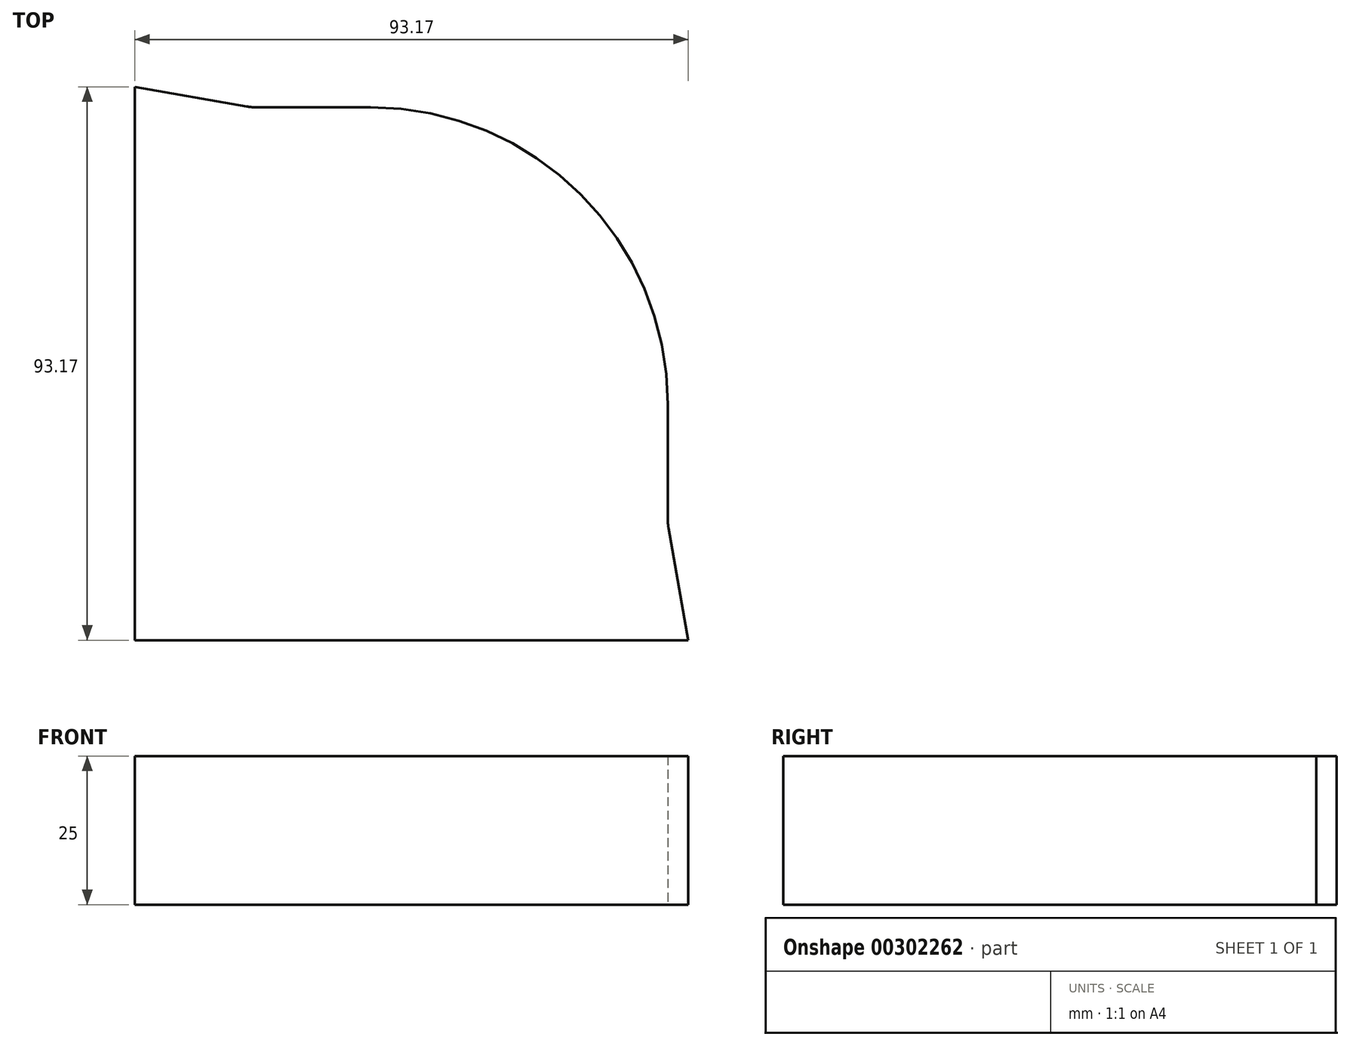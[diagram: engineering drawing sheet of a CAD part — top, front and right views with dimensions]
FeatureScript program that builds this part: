
annotation { "Feature Type Name" : "Feature", "Feature Type Description" : "" }
export const myFeature = defineFeature(function(context is Context, id is Id, definition is map)
    precondition{}
    {
        {
            var Q0;
            Q0=qCreatedBy(makeId("Top.planeOp"),FACE);
            var sketch = newSketch(context, id + "F0", { "sketchPlane" : qUnion([Q0])});
            skLineSegment(sketch, "E0.bottom", {"start": v(0, 0) * mm, "end": v(50, 0) * mm, "construction": true});
            skLineSegment(sketch, "E0.top", {"start": v(0, 50) * mm, "end": v(50, 50) * mm, "construction": true});
            skLineSegment(sketch, "E0.left", {"start": v(0, 0) * mm, "end": v(0, 50) * mm, "construction": true});
            skLineSegment(sketch, "E0.right", {"start": v(50, 0) * mm, "end": v(50, 50) * mm, "construction": true});
            skLineSegment(sketch, "E1", {"start": v(50, 0) * mm, "end": v(50, -19.13) * mm});
            skLineSegment(sketch, "E2", {"start": v(50.15, -20.86) * mm, "end": v(53.47, -39.7) * mm});
            skPoint(sketch, "E3.visualSharp", {"position": v(50, -20) * mm});
            skArc(sketch, "E3.filletArc", {"start": v(50, -19.13) * mm, "mid": v(50.04, -20) * mm, "end": v(50.15, -20.86) * mm});
            skLineSegment(sketch, "E4", {"start": v(50, -19.13) * mm, "end": v(0, -19.13) * mm});
            skLineSegment(sketch, "E5", {"start": v(0, 0) * mm, "end": v(50, 50) * mm, "construction": true});
            skArc(sketch, "E6", {"start": v(50, 0) * mm, "mid": v(46.2, 19.13) * mm, "end": v(35.36, 35.36) * mm});
            skLineSegment(sketch, "E7", {"start": v(0, 0) * mm, "end": v(-75.28, -75.28) * mm, "construction": true});
            skLineSegment(sketch, "E8", {"start": v(53.47, -39.7) * mm, "end": v(-39.7, -39.7) * mm});
            skArc(sketch, "E9.MirrorCS", {"start": v(-19.13, 50) * mm, "mid": v(-20, 50.04) * mm, "end": v(-20.86, 50.15) * mm});
            skLineSegment(sketch, "E10.MirrorCS", {"start": v(-20.86, 50.15) * mm, "end": v(-39.7, 53.47) * mm});
            skLineSegment(sketch, "E11.MirrorCS", {"start": v(-19.13, 50) * mm, "end": v(-19.13, 0) * mm});
            skArc(sketch, "E12.MirrorCS", {"start": v(0, 50) * mm, "mid": v(19.13, 46.2) * mm, "end": v(35.36, 35.36) * mm});
            skLineSegment(sketch, "E13.MirrorCS", {"start": v(-39.7, 53.47) * mm, "end": v(-39.7, -39.7) * mm});
            skLineSegment(sketch, "E14.MirrorCS", {"start": v(0, 50) * mm, "end": v(-19.13, 50) * mm});
            skPoint(sketch, "E15.MirrorP", {"position": v(-20, 50) * mm});
            skLineSegment(sketch, "E16", {"start": v(50, 0) * mm, "end": v(20, 0) * mm});
            skLineSegment(sketch, "E17.MirrorCS", {"start": v(0, 50) * mm, "end": v(0, 20) * mm});
            skSolve(sketch);
        }
        {
            var Q0;
            Q0 = qSketchRegion(id + "F0", true);
            extrude(context, id + "F1", {"entities" : qUnion([Q0]), "depth" : 25 * mm});
        }
    });
